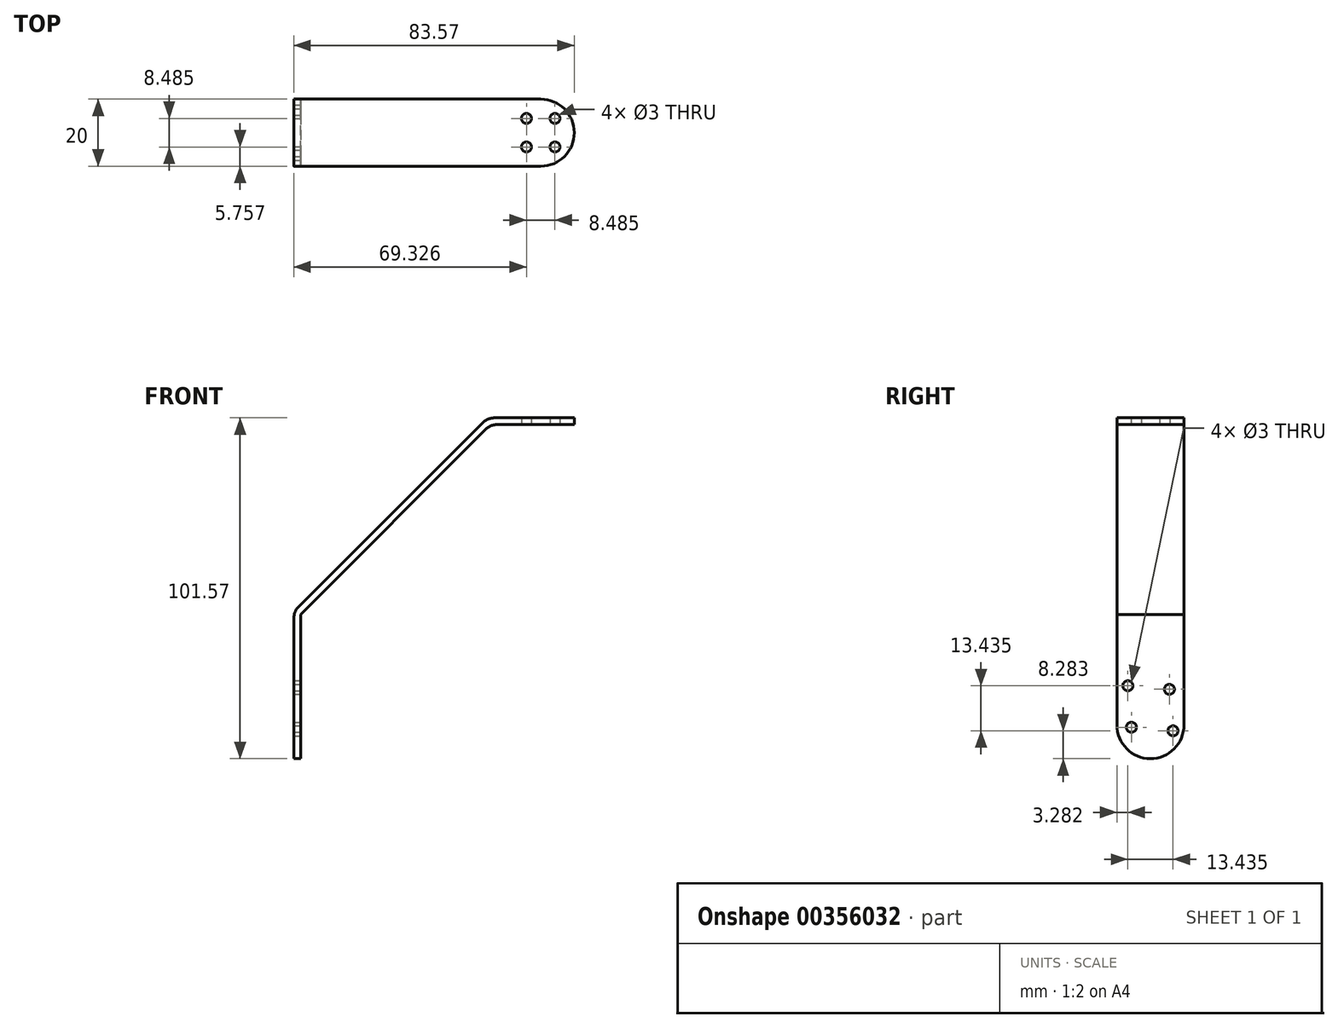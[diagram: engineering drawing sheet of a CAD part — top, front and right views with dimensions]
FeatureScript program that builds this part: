
annotation { "Feature Type Name" : "Feature", "Feature Type Description" : "" }
export const myFeature = defineFeature(function(context is Context, id is Id, definition is map)
    precondition{}
    {
        {
            var Q0;
            Q0=qCreatedBy(makeId("Front.planeOp"),FACE);
            var sketch = newSketch(context, id + "F0", { "sketchPlane" : qUnion([Q0])});
            skLineSegment(sketch, "E0", {"start": v(0, 0) * mm, "end": v(0, 43) * mm});
            skLineSegment(sketch, "E1", {"start": v(0, 43) * mm, "end": v(56.57, 99.57) * mm});
            skLineSegment(sketch, "E2", {"start": v(56.57, 99.57) * mm, "end": v(81.57, 99.57) * mm});
            skLineSegment(sketch, "E3.0", {"start": v(55.74, 101.57) * mm, "end": v(81.57, 101.57) * mm});
            skLineSegment(sketch, "E3.1", {"start": v(-2, 43.83) * mm, "end": v(55.74, 101.57) * mm});
            skLineSegment(sketch, "E3.2", {"start": v(-2, 0) * mm, "end": v(-2, 43.83) * mm});
            skLineSegment(sketch, "E4", {"start": v(81.57, 101.57) * mm, "end": v(81.57, 99.57) * mm});
            skLineSegment(sketch, "E5", {"start": v(0, 0) * mm, "end": v(-2, 0) * mm});
            skSolve(sketch);
        }
        {
            var Q0;
            Q0=makeQuery(id+"F0.imprint","IMPRINT",FACE,{"disambiguationData":[TD([[makeQuery(id+"F0.imprint","IMPRINT",EDGE,{"derivedFrom":sQuery(id+"F0.wireOp",EDGE,"E0")}),1.0]])]});
            extrude(context, id + "F1", {"entities" : qUnion([Q0]), "depth" : 20 * mm});
        }
        {
            var Q0;
            Q0=makeQuery(id+"F1.opExtrude","SWEPT_FACE",FACE,{"disambiguationData":[OSD([sQuery(id+"F0.wireOp",EDGE,"E2")])]});
            var sketch = newSketch(context, id + "F2", { "sketchPlane" : qUnion([Q0])});
            skLineSegment(sketch, "E6", {"start": v(71.57, 20) * mm, "end": v(71.57, 0) * mm, "construction": true});
            skLineSegment(sketch, "E7", {"start": v(81.57, 10) * mm, "end": v(71.57, 10) * mm, "construction": true});
            skPoint(sketch, "E8", {"position": v(77.57, 10) * mm});
            skPoint(sketch, "E9", {"position": v(71.57, 10) * mm});
            skPoint(sketch, "E10.1.0", {"position": v(75.81, 14.24) * mm});
            skPoint(sketch, "E10.3.0", {"position": v(67.33, 14.24) * mm});
            skPoint(sketch, "E10.5.0", {"position": v(67.33, 5.76) * mm});
            skPoint(sketch, "E10.7.0", {"position": v(75.81, 5.76) * mm});
            skSolve(sketch);
        }
        {
            var Q0;
            Q0=makeQuery(id+"F1.opExtrude","CAP_EDGE",EDGE,{"disambiguationData":[OSD([sQuery(id+"F0.wireOp",EDGE,"E5")])],"isStart":false});
            var Q1;
            Q1=makeQuery(id+"F1.opExtrude","CAP_EDGE",EDGE,{"disambiguationData":[OSD([sQuery(id+"F0.wireOp",EDGE,"E5")])],"isStart":true});
            var Q2;
            Q2=makeQuery(id+"F1.opExtrude","CAP_EDGE",EDGE,{"disambiguationData":[OSD([sQuery(id+"F0.wireOp",EDGE,"E4")])],"isStart":true});
            var Q3;
            Q3=makeQuery(id+"F1.opExtrude","CAP_EDGE",EDGE,{"disambiguationData":[OSD([sQuery(id+"F0.wireOp",EDGE,"E4")])],"isStart":false});
            fillet(context, id + "F3", {"entities" : qUnion([Q0, Q1, Q2, Q3]), "radius" : 10 * mm, "tangentPropagation" : true, "allowEdgeOverflow" : false});
        }
        {
            var Q0;
            Q0=sQuery(id+"F2.wireOp",VERTEX,"E10.1.0");
            var Q1;
            Q1=sQuery(id+"F2.wireOp",VERTEX,"E10.3.0");
            var Q2;
            Q2=sQuery(id+"F2.wireOp",VERTEX,"E10.5.0");
            var Q3;
            Q3=sQuery(id+"F2.wireOp",VERTEX,"E10.7.0");
            var Q4;
            Q4=makeQuery(id+"F1.opExtrude","SWEPT_BODY",BODY,{"disambiguationData":[OSD([sQuery(id+"F0.wireOp",EDGE,"E0"),sQuery(id+"F0.wireOp",EDGE,"E1"),sQuery(id+"F0.wireOp",EDGE,"E2"),sQuery(id+"F0.wireOp",EDGE,"E3.0"),sQuery(id+"F0.wireOp",EDGE,"E3.1"),sQuery(id+"F0.wireOp",EDGE,"E3.2"),sQuery(id+"F0.wireOp",EDGE,"E4"),sQuery(id+"F0.wireOp",EDGE,"E5")])]});
            hole(context, id + "F4", {"style" : HoleStyle.SIMPLE, "endStyle" : HoleEndStyle.THROUGH, "holeDiameter" : 3 * mm, "tappedDepth" : 4 * mm, "tapClearance" : 3, "locations" : qUnion([Q0, Q1, Q2, Q3]), "scope" : qUnion([Q4])});
        }
        {
            var Q0;
            Q0=makeQuery(id+"F1.opExtrude","CAP_EDGE",EDGE,{"disambiguationData":[OSD([sQuery(id+"F0.wireOp",EDGE,"E5")])],"isStart":true});
            var Q1;
            Q1=makeQuery(id+"F1.opExtrude","CAP_EDGE",EDGE,{"disambiguationData":[OSD([sQuery(id+"F0.wireOp",EDGE,"E5")])],"isStart":false});
            var Q2;
            Q2=makeQuery(id+"F1.opExtrude","SWEPT_EDGE",EDGE,{"disambiguationData":[OSD([sQuery(id+"F0.wireOp",EDGE,"E3.0"),sQuery(id+"F0.wireOp",EDGE,"E3.1")])]});
            var Q3;
            Q3=makeQuery(id+"F1.opExtrude","SWEPT_EDGE",EDGE,{"disambiguationData":[OSD([sQuery(id+"F0.wireOp",EDGE,"E1"),sQuery(id+"F0.wireOp",EDGE,"E2")])]});
            var Q4;
            Q4=makeQuery(id+"F1.opExtrude","SWEPT_EDGE",EDGE,{"disambiguationData":[OSD([sQuery(id+"F0.wireOp",EDGE,"E3.1"),sQuery(id+"F0.wireOp",EDGE,"E3.2")])]});
            fillet(context, id + "F5", {"entities" : qUnion([Q0, Q1, Q2, Q3, Q4]), "radius" : 5 * mm, "allowEdgeOverflow" : false});
        }
        {
            var Q0;
            Q0=makeQuery(id+"F1.opExtrude","SWEPT_FACE",FACE,{"disambiguationData":[OSD([sQuery(id+"F0.wireOp",EDGE,"E0")])]});
            var sketch = newSketch(context, id + "F6", { "sketchPlane" : qUnion([Q0])});
            skLineSegment(sketch, "E11", {"start": v(-10, 30) * mm, "end": v(-10, 0) * mm});
            skPoint(sketch, "E12", {"position": v(-10, 15) * mm});
            skPoint(sketch, "E13", {"position": v(-10, 23) * mm});
            skPoint(sketch, "E14.3.0", {"position": v(-15.66, 9.34) * mm});
            skPoint(sketch, "E14.7.0", {"position": v(-4.34, 20.66) * mm});
            skPoint(sketch, "E15", {"position": v(-10, 5.5) * mm});
            skPoint(sketch, "E16.1.0", {"position": v(-3.28, 8.28) * mm});
            skPoint(sketch, "E16.5.0", {"position": v(-16.72, 21.72) * mm});
            skSolve(sketch);
        }
        {
            var Q0;
            Q0=sQuery(id+"F6.wireOp",VERTEX,"E14.7.0");
            var Q1;
            Q1=sQuery(id+"F6.wireOp",VERTEX,"E16.5.0");
            var Q2;
            Q2=sQuery(id+"F6.wireOp",VERTEX,"E14.3.0");
            var Q3;
            Q3=sQuery(id+"F6.wireOp",VERTEX,"E16.1.0");
            var Q4;
            Q4=makeQuery(id+"F1.opExtrude","SWEPT_BODY",BODY,{"disambiguationData":[OSD([sQuery(id+"F0.wireOp",EDGE,"E0"),sQuery(id+"F0.wireOp",EDGE,"E1"),sQuery(id+"F0.wireOp",EDGE,"E2"),sQuery(id+"F0.wireOp",EDGE,"E3.0"),sQuery(id+"F0.wireOp",EDGE,"E3.1"),sQuery(id+"F0.wireOp",EDGE,"E3.2"),sQuery(id+"F0.wireOp",EDGE,"E4"),sQuery(id+"F0.wireOp",EDGE,"E5")])]});
            hole(context, id + "F7", {"style" : HoleStyle.SIMPLE, "endStyle" : HoleEndStyle.THROUGH, "holeDiameter" : 3 * mm, "tappedDepth" : 4 * mm, "tapClearance" : 3, "locations" : qUnion([Q0, Q1, Q2, Q3]), "scope" : qUnion([Q4])});
        }
        {
            var Q0;
            Q0=makeQuery(id+"F1.opExtrude","SWEPT_FACE",FACE,{"disambiguationData":[OSD([sQuery(id+"F0.wireOp",EDGE,"E1")])]});
            var sketch = newSketch(context, id + "F8", { "sketchPlane" : qUnion([Q0])});
            skLineSegment(sketch, "E17.bottom", {"start": v(37.6, 5) * mm, "end": v(41.6, 5) * mm});
            skLineSegment(sketch, "E17.top", {"start": v(37.6, 15) * mm, "end": v(41.6, 15) * mm});
            skLineSegment(sketch, "E17.left", {"start": v(37.6, 5) * mm, "end": v(37.6, 15) * mm});
            skLineSegment(sketch, "E17.right", {"start": v(41.6, 5) * mm, "end": v(41.6, 15) * mm});
            skSolve(sketch);
        }
        {
            var Q0;
            Q0=makeQuery(id+"F8.imprint","IMPRINT",FACE,{"disambiguationData":[TD([[makeQuery(id+"F8.imprint","IMPRINT",EDGE,{"derivedFrom":sQuery(id+"F8.wireOp",EDGE,"E17.bottom")}),1.0]])]});
            extrude(context, id + "F9", {"entities" : qUnion([Q0]), "operationType" : NewBodyOperationType.REMOVE, "oppositeDirection" : true, "depth" : 25 * mm});
        }
    });
